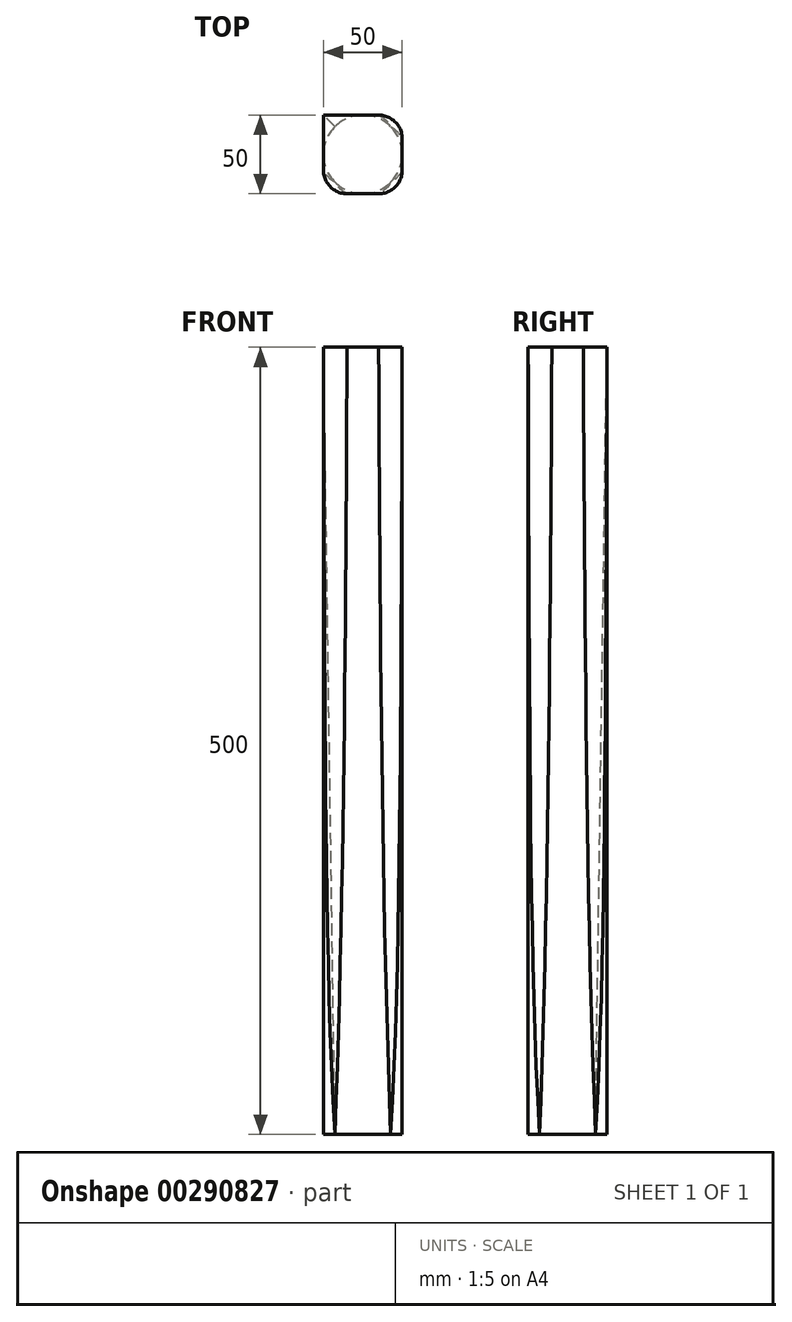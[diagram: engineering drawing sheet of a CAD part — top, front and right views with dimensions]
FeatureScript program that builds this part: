
annotation { "Feature Type Name" : "Feature", "Feature Type Description" : "" }
export const myFeature = defineFeature(function(context is Context, id is Id, definition is map)
    precondition{}
    {
        {
            var Q0;
            Q0=qCreatedBy(makeId("Top.planeOp"),FACE);
            var sketch = newSketch(context, id + "F0", { "sketchPlane" : qUnion([Q0])});
            skCircle(sketch, "E0", {"center": v(0, 0) * mm, "radius": 25 * mm});
            skSolve(sketch);
        }
        {
            var Q0;
            Q0=qCreatedBy(makeId("Top.planeOp"),FACE);
            cPlane(context, id + "F1", {"entities" : qUnion([Q0]), "cplaneType" : CPlaneType.OFFSET, "offset" : 500 * mm, "width" : 150 * mm, "height" : 150 * mm});
        }
        {
            var Q0;
            Q0=qCreatedBy(id+"F1.planeOp",FACE);
            var sketch = newSketch(context, id + "F2", { "sketchPlane" : qUnion([Q0])});
            skLineSegment(sketch, "E1.bottom", {"start": v(25, 25) * mm, "end": v(-25, 25) * mm});
            skLineSegment(sketch, "E1.top", {"start": v(25, -25) * mm, "end": v(-25, -25) * mm});
            skLineSegment(sketch, "E1.left", {"start": v(25, 25) * mm, "end": v(25, -25) * mm});
            skLineSegment(sketch, "E1.right", {"start": v(-25, 25) * mm, "end": v(-25, -25) * mm});
            skPoint(sketch, "E1.middle", {"position": v(0, 0) * mm});
            skSolve(sketch);
        }
        {
            var Q0;
            Q0=makeQuery(id+"F0.imprint","IMPRINT",FACE,{"disambiguationData":[TD([[makeQuery(id+"F0.imprint","IMPRINT",EDGE,{"derivedFrom":sQuery(id+"F0.wireOp",EDGE,"E0")}),1.0]])]});
            var Q1;
            Q1=makeQuery(id+"F2.imprint","IMPRINT",FACE,{"disambiguationData":[TD([[makeQuery(id+"F2.imprint","IMPRINT",EDGE,{"derivedFrom":sQuery(id+"F2.wireOp",EDGE,"E1.bottom")}),1.0]])]});
            loft(context, id + "F3", {"sheetProfilesArray" : [{ "sheetProfileEntities" : qUnion([Q0]) }, { "sheetProfileEntities" : qUnion([Q1]) }]});
        }
        {
            var Q0;
            Q0=makeQuery(id+"F3.opLoft","SWEPT_EDGE",EDGE,{"disambiguationData":[OSD([sQuery(id+"F0.wireOp",EDGE,"E0"),sQuery(id+"F2.wireOp",EDGE,"E1.top"),sQuery(id+"F2.wireOp",EDGE,"E1.left"),sQuery(id+"F2.wireOp",EDGE,"E1.right")])]});
            var Q1;
            Q1=makeQuery(id+"F3.opLoft","SWEPT_EDGE",EDGE,{"disambiguationData":[OSD([sQuery(id+"F0.wireOp",EDGE,"E0"),sQuery(id+"F2.wireOp",EDGE,"E1.bottom"),sQuery(id+"F2.wireOp",EDGE,"E1.top"),sQuery(id+"F2.wireOp",EDGE,"E1.right")])]});
            var Q2;
            Q2=makeQuery(id+"F3.opLoft","SWEPT_EDGE",EDGE,{"disambiguationData":[OSD([sQuery(id+"F2.wireOp",EDGE,"E1.bottom"),sQuery(id+"F2.wireOp",EDGE,"E1.left")])]});
            var Q3;
            Q3=makeQuery(id+"F3.opLoft","SWEPT_EDGE",EDGE,{"disambiguationData":[OSD([sQuery(id+"F0.wireOp",EDGE,"E0"),sQuery(id+"F2.wireOp",EDGE,"E1.bottom"),sQuery(id+"F2.wireOp",EDGE,"E1.left"),sQuery(id+"F2.wireOp",EDGE,"E1.right")])]});
            fillet(context, id + "F4", {"entities" : qUnion([Q0, Q1, Q2, Q3]), "radius" : 15 * mm, "tangentPropagation" : true, "allowEdgeOverflow" : false});
        }
    });
